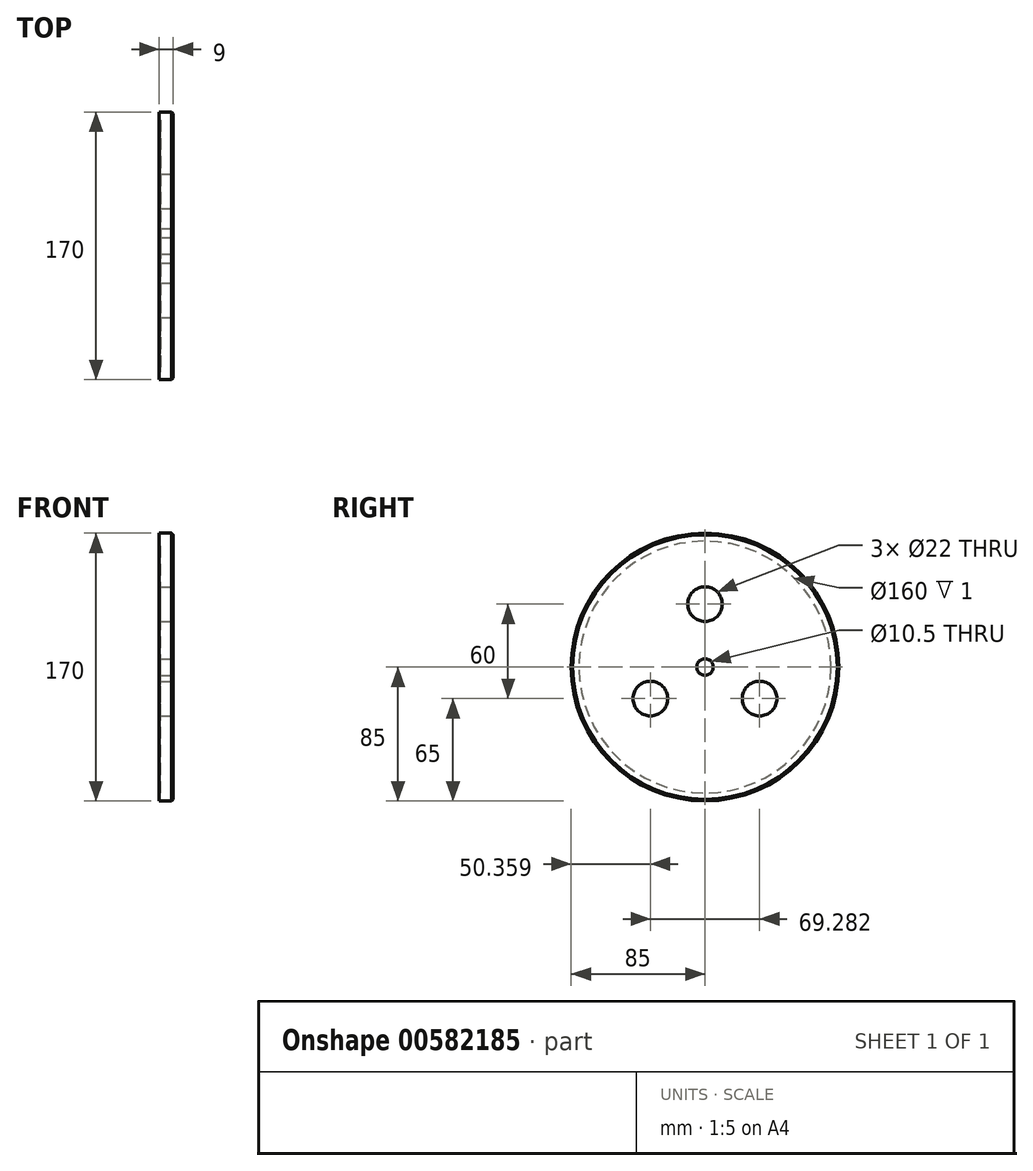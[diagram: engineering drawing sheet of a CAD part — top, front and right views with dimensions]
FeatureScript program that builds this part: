
annotation { "Feature Type Name" : "Feature", "Feature Type Description" : "" }
export const myFeature = defineFeature(function(context is Context, id is Id, definition is map)
    precondition{}
    {
        {
            var Q0;
            Q0=qCreatedBy(makeId("Front.planeOp"),FACE);
            var sketch = newSketch(context, id + "F0", { "sketchPlane" : qUnion([Q0])});
            skLineSegment(sketch, "E0", {"start": v(0, 80) * mm, "end": v(0, 85) * mm});
            skLineSegment(sketch, "E1", {"start": v(0, 85) * mm, "end": v(9, 85) * mm});
            skLineSegment(sketch, "E2", {"start": v(9, 85) * mm, "end": v(9, 0) * mm});
            skLineSegment(sketch, "E3", {"start": v(9, 0) * mm, "end": v(1, 0) * mm});
            skLineSegment(sketch, "E4", {"start": v(1, 0) * mm, "end": v(1, 80) * mm});
            skLineSegment(sketch, "E5", {"start": v(1, 80) * mm, "end": v(0, 80) * mm});
            skSolve(sketch);
        }
        {
            var Q0;
            Q0=qSketchRegion(id+"F0",true);
            var Q1;
            Q1=sQuery(id+"F0.wireOp",EDGE,"E3");
            revolve(context, id + "F1", {"entities" : qUnion([Q0]), "axis" : qUnion([Q1]), "revolveType" : RevolveType.FULL});
        }
        {
            var Q0;
            Q0=makeQuery(id+"F1.opRevolve","SWEPT_FACE",FACE,{"disambiguationData":[OSD([sQuery(id+"F0.wireOp",EDGE,"E2")])]});
            var sketch = newSketch(context, id + "F2", { "sketchPlane" : qUnion([Q0])});
            skPoint(sketch, "E6", {"position": v(0, 0) * mm});
            skSolve(sketch);
        }
        {
            var Q0;
            Q0=sQuery(id+"F2.wireOp",VERTEX,"E6");
            var Q1;
            Q1=makeQuery(id+"F1.opRevolve","SWEPT_BODY",BODY,{"disambiguationData":[OSD([sQuery(id+"F0.wireOp",EDGE,"E0"),sQuery(id+"F0.wireOp",EDGE,"E1"),sQuery(id+"F0.wireOp",EDGE,"E2"),sQuery(id+"F0.wireOp",EDGE,"E3"),sQuery(id+"F0.wireOp",EDGE,"E4"),sQuery(id+"F0.wireOp",EDGE,"E5")])]});
            hole(context, id + "F3", {"style" : HoleStyle.SIMPLE, "endStyle" : HoleEndStyle.THROUGH, "standardTappedOrClearance" : lookupTablePath({ "standard" : "ISO", "fit" : "Close", "size" : "M10", "type" : "Clearance" }), "standardBlindInLast" : lookupTablePath({ "fit" : "Close", "standard" : "ISO", "size" : "M10", "type" : "Clearance" }), "holeDiameter" : 10.5 * mm, "tappedDepth" : 15.25 * mm, "tapClearance" : 3, "locations" : qUnion([Q0]), "scope" : qUnion([Q1])});
        }
        {
            var Q0;
            Q0=makeQuery(id+"F1.opRevolve","SWEPT_FACE",FACE,{"disambiguationData":[OSD([sQuery(id+"F0.wireOp",EDGE,"E2")])]});
            var sketch = newSketch(context, id + "F4", { "sketchPlane" : qUnion([Q0])});
            skPoint(sketch, "E7", {"position": v(0, 40) * mm});
            skPoint(sketch, "E8.1.0", {"position": v(-34.64, -20) * mm});
            skPoint(sketch, "E8.2.0", {"position": v(34.64, -20) * mm});
            skPoint(sketch, "E8.center", {"position": v(0, 0) * mm});
            skSolve(sketch);
        }
        {
            var Q0;
            Q0=sQuery(id+"F4.wireOp",VERTEX,"E7");
            var Q1;
            Q1=sQuery(id+"F4.wireOp",VERTEX,"E8.2.0");
            var Q2;
            Q2=sQuery(id+"F4.wireOp",VERTEX,"E8.1.0");
            var Q3;
            Q3=makeQuery(id+"F1.opRevolve","SWEPT_BODY",BODY,{"disambiguationData":[OSD([sQuery(id+"F0.wireOp",EDGE,"E0"),sQuery(id+"F0.wireOp",EDGE,"E1"),sQuery(id+"F0.wireOp",EDGE,"E2"),sQuery(id+"F0.wireOp",EDGE,"E3"),sQuery(id+"F0.wireOp",EDGE,"E4"),sQuery(id+"F0.wireOp",EDGE,"E5")])]});
            hole(context, id + "F5", {"style" : HoleStyle.SIMPLE, "endStyle" : HoleEndStyle.THROUGH, "holeDiameter" : 22 * mm, "tappedDepth" : 15.25 * mm, "tapClearance" : 3, "locations" : qUnion([Q0, Q1, Q2]), "scope" : qUnion([Q3])});
        }
        {
            var Q0;
            Q0=makeQuery(id+"F1.opRevolve","SWEPT_EDGE",EDGE,{"disambiguationData":[OSD([sQuery(id+"F0.wireOp",EDGE,"E1"),sQuery(id+"F0.wireOp",EDGE,"E2")])]});
            var Q1;
            Q1=makeQuery(id+"F5.hole-2.boolean.opBoolean","COPY",EDGE,{"derivedFrom":makeQuery(id+"F5.hole-2.opRevolve","SWEPT_EDGE",EDGE,{"disambiguationData":[OSD([sQuery(id+"F5.hole-2.sketch.wireOp",EDGE,"core_line_2"),sQuery(id+"F5.hole-2.sketch.wireOp",EDGE,"core_line_3")])]})});
            var Q2;
            Q2=makeQuery(id+"F5.hole-2.boolean.opBoolean","INTERSECT",EDGE,{"derivedFrom":[makeQuery(id+"F1.opRevolve","SWEPT_FACE",FACE,{"disambiguationData":[OSD([sQuery(id+"F0.wireOp",EDGE,"E4")])]}),makeQuery(id+"F5.hole-2.opRevolve","SWEPT_FACE",FACE,{"disambiguationData":[OSD([sQuery(id+"F5.hole-2.sketch.wireOp",EDGE,"core_line_2")])]})]});
            var Q3;
            Q3=makeQuery(id+"F5.hole-1.boolean.opBoolean","INTERSECT",EDGE,{"derivedFrom":[makeQuery(id+"F1.opRevolve","SWEPT_FACE",FACE,{"disambiguationData":[OSD([sQuery(id+"F0.wireOp",EDGE,"E4")])]}),makeQuery(id+"F5.hole-1.opRevolve","SWEPT_FACE",FACE,{"disambiguationData":[OSD([sQuery(id+"F5.hole-1.sketch.wireOp",EDGE,"core_line_2")])]})]});
            var Q4;
            Q4=makeQuery(id+"F5.hole-1.boolean.opBoolean","COPY",EDGE,{"derivedFrom":makeQuery(id+"F5.hole-1.opRevolve","SWEPT_EDGE",EDGE,{"disambiguationData":[OSD([sQuery(id+"F5.hole-1.sketch.wireOp",EDGE,"core_line_2"),sQuery(id+"F5.hole-1.sketch.wireOp",EDGE,"core_line_3")])]})});
            var Q5;
            Q5=makeQuery(id+"F5.hole-0.boolean.opBoolean","COPY",EDGE,{"derivedFrom":makeQuery(id+"F5.hole-0.opRevolve","SWEPT_EDGE",EDGE,{"disambiguationData":[OSD([sQuery(id+"F5.hole-0.sketch.wireOp",EDGE,"core_line_2"),sQuery(id+"F5.hole-0.sketch.wireOp",EDGE,"core_line_3")])]})});
            var Q6;
            Q6=makeQuery(id+"F5.hole-0.boolean.opBoolean","INTERSECT",EDGE,{"derivedFrom":[makeQuery(id+"F1.opRevolve","SWEPT_FACE",FACE,{"disambiguationData":[OSD([sQuery(id+"F0.wireOp",EDGE,"E4")])]}),makeQuery(id+"F5.hole-0.opRevolve","SWEPT_FACE",FACE,{"disambiguationData":[OSD([sQuery(id+"F5.hole-0.sketch.wireOp",EDGE,"core_line_2")])]})]});
            chamfer(context, id + "F6", {"entities" : qUnion([Q0, Q1, Q2, Q3, Q4, Q5, Q6]), "width" : 1 * mm, "tangentPropagation" : true});
        }
    });
